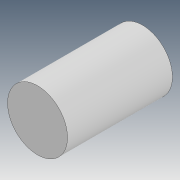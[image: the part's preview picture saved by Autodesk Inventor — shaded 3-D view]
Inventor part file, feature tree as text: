
AUTODESK INVENTOR PART (.ipt)
format: ipt  version: 2021 (Build 250183000, 183)  size: 78,848 bytes
history: native  units: in
note: dims shown in document units (in); Inventor stores cm internally (conversion verified against a paired STEP export)
features: sketch x2, other x1, extrude x1
ambient origin geometry x8: Origin, YZ Plane, XZ Plane, XY Plane, X Axis, Y Axis, Z Axis, Center Point
bodies: Body1 (feature_tree)
feature tree (4):
  other  "Sólido1"
  sketch  "Esboço1"  dims[d0=0.0787in d1=0.1378in d2=0.0in]
  extrude  "Extrusão1"  Depth=0.1378in TaperAngle=0.0deg
  sketch  "Esboço2"
